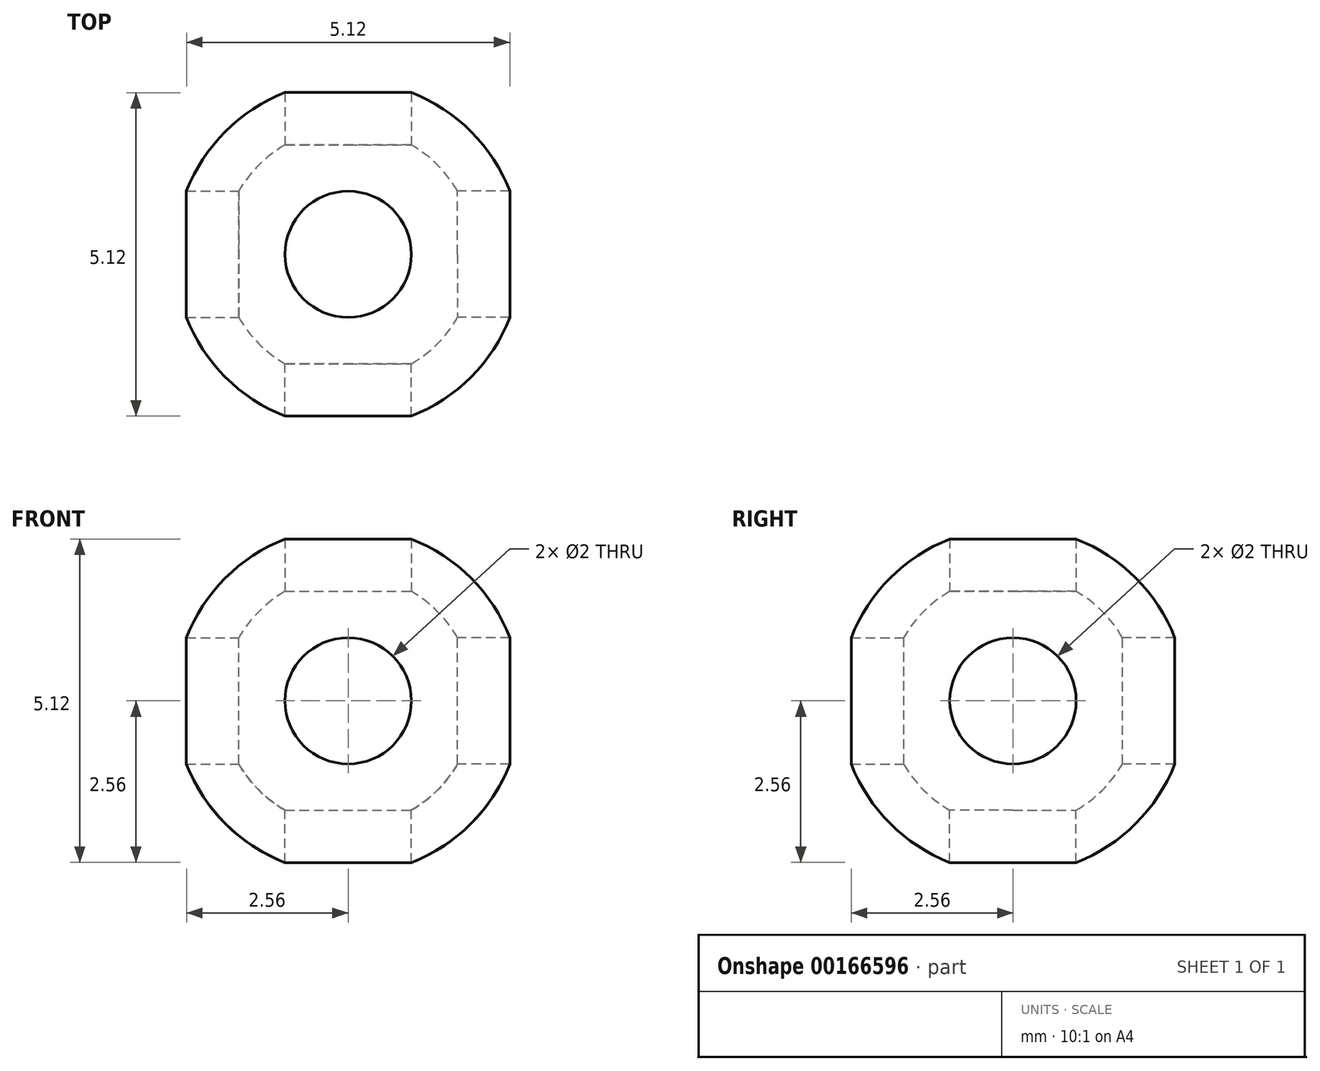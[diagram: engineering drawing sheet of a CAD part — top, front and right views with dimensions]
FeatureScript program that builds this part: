
annotation { "Feature Type Name" : "Feature", "Feature Type Description" : "" }
export const myFeature = defineFeature(function(context is Context, id is Id, definition is map)
    precondition{}
    {
        {
            var Q0;
            Q0=qCreatedBy(makeId("Top.planeOp"),FACE);
            var sketch = newSketch(context, id + "F0", { "sketchPlane" : qUnion([Q0])});
            skLineSegment(sketch, "E0", {"start": v(-3.23, 0) * mm, "end": v(3.44, 0) * mm});
            skArc(sketch, "E1", {"start": v(2.75, 0) * mm, "mid": v(0, 2.75) * mm, "end": v(-2.75, 0) * mm});
            skSolve(sketch);
        }
        {
            var Q0;
            {var subQ0=sQuery(id+"F0.wireOp",EDGE,"E1");Q0=makeQuery(id+"F0.imprint","IMPRINT",FACE,{"disambiguationData":[TD([[makeQuery(id+"F0.imprint","IMPRINT",EDGE,{"derivedFrom":subQ0}),1.0]])]});}
            var Q1;
            Q1=sQuery(id+"F0.wireOp",EDGE,"E0");
            revolve(context, id + "F1", {"entities" : qUnion([Q0]), "axis" : qUnion([Q1]), "revolveType" : RevolveType.FULL});
        }
        {
            var Q0;
            Q0=makeQuery(id+"F1.opRevolve","SWEPT_FACE",FACE,{"disambiguationData":[OSD([sQuery(id+"F0.wireOp",EDGE,"E1")])]});
            var Q1;
            Q1=makeQuery(id+"F1.opRevolve","SWEPT_BODY",BODY,{"disambiguationData":[OSD([sQuery(id+"F0.wireOp",EDGE,"E0"),sQuery(id+"F0.wireOp",EDGE,"E1")])]});
            shell(context, id + "F2", {"isHollow" : true, "entities" : qUnion([Q0]), "parts" : qUnion([Q1]), "thickness" : .75 * mm});
        }
        {
            var Q0;
            Q0=qCreatedBy(makeId("Top.planeOp"),FACE);
            var sketch = newSketch(context, id + "F3", { "sketchPlane" : qUnion([Q0])});
            skPoint(sketch, "E2", {"position": v(0, 0) * mm});
            skSolve(sketch);
        }
        {
            var Q0;
            Q0=sQuery(id+"F3.wireOp",VERTEX,"E2");
            var Q1;
            Q1=makeQuery(id+"F1.opRevolve","SWEPT_BODY",BODY,{"disambiguationData":[OSD([sQuery(id+"F0.wireOp",EDGE,"E0"),sQuery(id+"F0.wireOp",EDGE,"E1")])]});
            hole(context, id + "F4", {"style" : HoleStyle.SIMPLE, "endStyle" : HoleEndStyle.THROUGH, "holeDiameter" : 2 * mm, "locations" : qUnion([Q0]), "scope" : qUnion([Q1]), "isTappedThrough" : true});
        }
        {
            var Q0;
            Q0=qCreatedBy(makeId("Top.planeOp"),FACE);
            var sketch = newSketch(context, id + "F5", { "sketchPlane" : qUnion([Q0])});
            skPoint(sketch, "E3", {"position": v(0, 0) * mm});
            skSolve(sketch);
        }
        {
            var Q0;
            Q0=sQuery(id+"F5.wireOp",VERTEX,"E3");
            var Q1;
            Q1=makeQuery(id+"F1.opRevolve","SWEPT_BODY",BODY,{"disambiguationData":[OSD([sQuery(id+"F0.wireOp",EDGE,"E0"),sQuery(id+"F0.wireOp",EDGE,"E1")])]});
            hole(context, id + "F6", {"style" : HoleStyle.SIMPLE, "endStyle" : HoleEndStyle.THROUGH, "oppositeDirection" : true, "holeDiameter" : 2 * mm, "locations" : qUnion([Q0]), "scope" : qUnion([Q1]), "isTappedThrough" : true});
        }
        {
            var Q0;
            Q0=qCreatedBy(makeId("Right.planeOp"),FACE);
            var sketch = newSketch(context, id + "F7", { "sketchPlane" : qUnion([Q0])});
            skPoint(sketch, "E4", {"position": v(0, 0) * mm});
            skSolve(sketch);
        }
        {
            var Q0;
            Q0=sQuery(id+"F7.wireOp",VERTEX,"E4");
            var Q1;
            Q1=makeQuery(id+"F1.opRevolve","SWEPT_BODY",BODY,{"disambiguationData":[OSD([sQuery(id+"F0.wireOp",EDGE,"E0"),sQuery(id+"F0.wireOp",EDGE,"E1")])]});
            hole(context, id + "F8", {"style" : HoleStyle.SIMPLE, "endStyle" : HoleEndStyle.THROUGH, "holeDiameter" : 2 * mm, "locations" : qUnion([Q0]), "scope" : qUnion([Q1]), "isTappedThrough" : true});
        }
        {
            var Q0;
            Q0=qCreatedBy(makeId("Right.planeOp"),FACE);
            var sketch = newSketch(context, id + "F9", { "sketchPlane" : qUnion([Q0])});
            skPoint(sketch, "E5", {"position": v(0, 0) * mm});
            skSolve(sketch);
        }
        {
            var Q0;
            Q0=sQuery(id+"F9.wireOp",VERTEX,"E5");
            var Q1;
            Q1=makeQuery(id+"F1.opRevolve","SWEPT_BODY",BODY,{"disambiguationData":[OSD([sQuery(id+"F0.wireOp",EDGE,"E0"),sQuery(id+"F0.wireOp",EDGE,"E1")])]});
            hole(context, id + "F10", {"style" : HoleStyle.SIMPLE, "endStyle" : HoleEndStyle.THROUGH, "oppositeDirection" : true, "holeDiameter" : 2 * mm, "locations" : qUnion([Q0]), "scope" : qUnion([Q1]), "isTappedThrough" : true});
        }
        {
            var Q0;
            Q0=qCreatedBy(makeId("Front.planeOp"),FACE);
            var sketch = newSketch(context, id + "F11", { "sketchPlane" : qUnion([Q0])});
            skPoint(sketch, "E6", {"position": v(0, 0) * mm});
            skSolve(sketch);
        }
        {
            var Q0;
            Q0=sQuery(id+"F11.wireOp",VERTEX,"E6");
            var Q1;
            Q1=makeQuery(id+"F1.opRevolve","SWEPT_BODY",BODY,{"disambiguationData":[OSD([sQuery(id+"F0.wireOp",EDGE,"E0"),sQuery(id+"F0.wireOp",EDGE,"E1")])]});
            hole(context, id + "F12", {"style" : HoleStyle.SIMPLE, "endStyle" : HoleEndStyle.THROUGH, "holeDiameter" : 2 * mm, "locations" : qUnion([Q0]), "scope" : qUnion([Q1]), "isTappedThrough" : true});
        }
        {
            var Q0;
            Q0=qCreatedBy(makeId("Front.planeOp"),FACE);
            var sketch = newSketch(context, id + "F13", { "sketchPlane" : qUnion([Q0])});
            skPoint(sketch, "E7", {"position": v(0, 0) * mm});
            skSolve(sketch);
        }
        {
            var Q0;
            Q0=sQuery(id+"F13.wireOp",VERTEX,"E7");
            var Q1;
            Q1=makeQuery(id+"F1.opRevolve","SWEPT_BODY",BODY,{"disambiguationData":[OSD([sQuery(id+"F0.wireOp",EDGE,"E0"),sQuery(id+"F0.wireOp",EDGE,"E1")])]});
            hole(context, id + "F14", {"style" : HoleStyle.SIMPLE, "endStyle" : HoleEndStyle.THROUGH, "oppositeDirection" : true, "holeDiameter" : 2 * mm, "locations" : qUnion([Q0]), "scope" : qUnion([Q1]), "isTappedThrough" : true});
        }
    });
